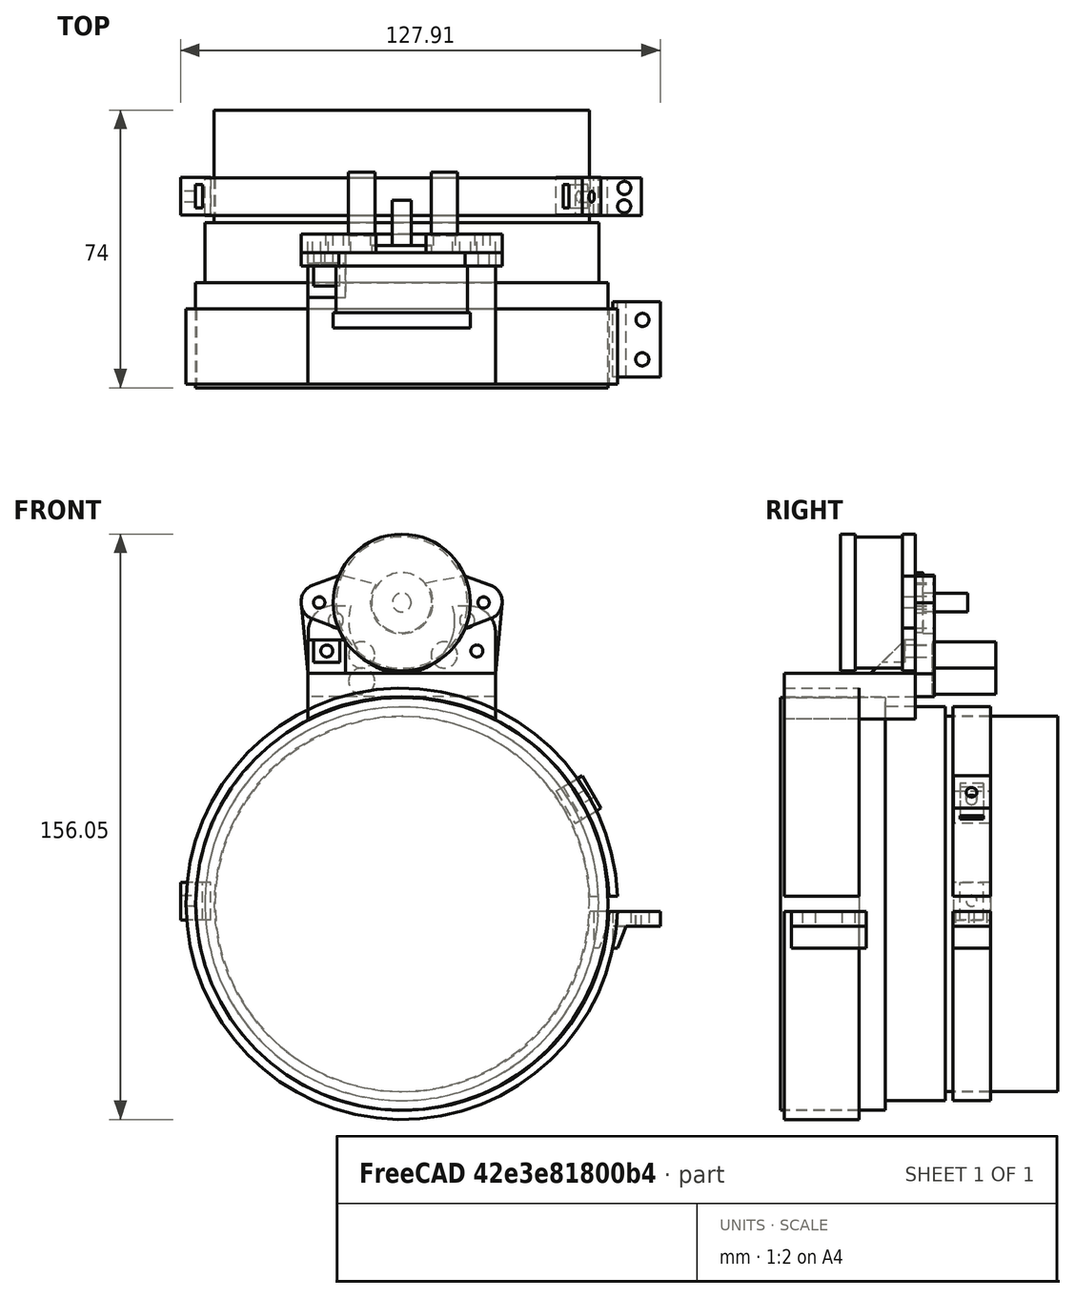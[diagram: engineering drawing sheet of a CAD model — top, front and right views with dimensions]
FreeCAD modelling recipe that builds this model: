
FCSTD DOCUMENT  (FreeCAD 0.18R4 (GitTag))
Label: MTO_3M_6A_500mm
License: All rights reserved
LicenseURL: http://en.wikipedia.org/wiki/All_rights_reserved
objects: Sketcher::SketchObject×30, PartDesign::Body×20, PartDesign::Pad×18, PartDesign::Pocket×12, PartDesign::FeatureBase×8, Mesh::Feature×1, PartDesign::Fillet×1, PartDesign::Plane×1
note: 120 computed .brp shape members not serialized (recipe doc carries the construction recipe); baked Part::Feature solids carry a one-line shape summary decoded from their .brp

FEATURE [Sketcher::SketchObject] Sketch
  MapMode = 5
  Support = -> [XY_Plane]
  sketch-geometry (1):
    g0: Circle CenterX=0.027552 CenterY=0 CenterZ=0 NormalX=0 NormalY=0 NormalZ=1 AngleXU=0 Radius=55
  constraints (1):
    c: Diameter(g0) = 110
FEATURE [PartDesign::Pad] Pad
  Length = 28
  Length2 = 100
  Profile = -> Sketch
  Type = 0
FEATURE [Sketcher::SketchObject] Sketch001
  MapMode = 5
  Placement = pos=(0,0,28) rot=(0,0,1;0rad)
  Support = -> [Pad]
  sketch-geometry (1):
    g0: Circle CenterX=0 CenterY=0 CenterZ=0 NormalX=0 NormalY=0 NormalZ=1 AngleXU=0 Radius=52.5
  constraints (2):
    c: Coincident(g0,g-1)
    c: Diameter(g0) = 105
FEATURE [PartDesign::Pad] Pad001
  BaseFeature = -> Pad
  Length = 16
  Length2 = 100
  Profile = -> Sketch001
  Type = 0
FEATURE [Sketcher::SketchObject] Sketch002
  MapMode = 5
  Placement = pos=(0,0,0) rot=(1,0,0;1.5708rad)
  Support = -> [XZ_Plane001]
  sketch-geometry (1):
    g0: Circle CenterX=0 CenterY=0 CenterZ=0 NormalX=0 NormalY=0 NormalZ=1 AngleXU=0 Radius=57.5
  constraints (2):
    c: Coincident(g0,g-1)
    c: Diameter(g0) = 115
FEATURE [PartDesign::Pad] Pad002
  Length = 20
  Length2 = 100
  Placement = pos=(0,0,0) rot=(1,0,0;1.5708rad)
  Profile = -> Sketch002
  Type = 0
FEATURE [Sketcher::SketchObject] Sketch003
  MapMode = 5
  Placement = pos=(0,-20,8.8e-15) rot=(1,0,0;1.5708rad)
  Support = -> [Pad002]
  sketch-geometry (1):
    g0: Circle CenterX=0.237796 CenterY=-0.12528 CenterZ=0 NormalX=0 NormalY=0 NormalZ=1 AngleXU=0 Radius=55
  constraints (1):
    c: Diameter(g0) = 110
FEATURE [PartDesign::Pocket] Pocket
  BaseFeature = -> Pad002
  Length = 25
  Length2 = 100
  Placement = pos=(0,0,0) rot=(1,0,0;1.5708rad)
  Profile = -> Sketch003
  Type = 0
FEATURE [Sketcher::SketchObject] Sketch004
  MapMode = 5
  Placement = pos=(0,-20,8.8e-15) rot=(1,0,0;1.5708rad)
  Support = -> [Pocket]
  sketch-geometry (4):
    g0: LineSegment StartX=65.8967 StartY=-2 StartZ=0 EndX=0 EndY=-2 EndZ=0
    g1: LineSegment StartX=0 StartY=-2 StartZ=0 EndX=0 EndY=2 EndZ=0
    g2: LineSegment StartX=0 StartY=2 StartZ=0 EndX=65.8967 EndY=2 EndZ=0
    g3: LineSegment StartX=65.8967 StartY=2 StartZ=0 EndX=65.8967 EndY=-2 EndZ=0
  constraints (10):
    c: Coincident(g0,g1)
    c: Coincident(g1,g2)
    c: Coincident(g2,g3)
    c: Coincident(g3,g0)
    c: Horizontal(g0)
    c: Horizontal(g2)
    c: Vertical(g1)
    c: Vertical(g3)
    c: DistanceY(g1,g1) = 4
    c: Symmetric(g0,g1,g-1)
FEATURE [PartDesign::Pocket] Pocket001
  BaseFeature = -> Pocket
  Length = 21
  Length2 = 100
  Placement = pos=(0,0,0) rot=(1,0,0;1.5708rad)
  Profile = -> Sketch004
  Type = 0
FEATURE [PartDesign::Body] Body001  label="01_StepperRing"
  Group = -> [Sketch002,Pad002,Sketch003,Pocket,Sketch004,Pocket001]
  Origin = -> Origin001
  Placement = pos=(0,-2,0) rot=(0,0,1;0rad)
  Tip = -> Pocket001
FEATURE [Mesh::Feature] StepperMotor_scaled  label="REFERENCE_StepperMotor"
  Placement = pos=(-0.0857864,9.5,75.5711) rot=(0,-0.707107,-0.707107;3.14159rad)
FEATURE [Sketcher::SketchObject] Sketch012
  MapMode = 5
  Placement = pos=(0,0,44) rot=(0,0,1;0rad)
  Support = -> [Pad001]
  sketch-geometry (1):
    g0: Circle CenterX=0 CenterY=0 CenterZ=0 NormalX=0 NormalY=0 NormalZ=1 AngleXU=0 Radius=50
  constraints (2):
    c: Coincident(g0,g-1)
    c: Diameter(g0) = 100
FEATURE [PartDesign::Pad] Pad005
  BaseFeature = -> Pad001
  Length = 30
  Length2 = 100
  Profile = -> Sketch012
  Type = 0
FEATURE [PartDesign::Body] Body  label="REFERENCE_Lens"
  Group = -> [Sketch,Pad,Sketch001,Pad001,Sketch012,Pad005]
  Origin = -> Origin
  Placement = pos=(0,-23,5e-15) rot=(-1,0,0;1.5708rad)
  Tip = -> Pad005
FEATURE [Sketcher::SketchObject] Sketch013
  MapMode = 5
  Placement = pos=(0,0,0) rot=(1,0,0;1.5708rad)
  Support = -> [XZ_Plane002]
  sketch-geometry (6):
    g0: LineSegment StartX=68.9137 StartY=6.14746 StartZ=0 EndX=68.9137 EndY=2.14746 EndZ=0
    g1: LineSegment StartX=68.9137 StartY=2.14746 StartZ=0 EndX=56.1787 EndY=2.14746 EndZ=0
    g2: LineSegment StartX=56.1787 StartY=2.14746 StartZ=0 EndX=56.1787 EndY=11.9606 EndZ=0
    g3: LineSegment StartX=68.9137 StartY=6.14746 StartZ=0 EndX=59.8276 EndY=6.14746 EndZ=0
    g4: LineSegment StartX=59.8276 StartY=6.14746 StartZ=0 EndX=57.5381 EndY=11.9606 EndZ=0
    g5: LineSegment StartX=57.5381 StartY=11.9606 StartZ=0 EndX=56.1787 EndY=11.9606 EndZ=0
  constraints (12):
    c: Coincident(g0,g1)
    c: Coincident(g1,g2)
    c: Horizontal(g1)
    c: Vertical(g0)
    c: Vertical(g2)
    c: DistanceY(g0,g0) = 4
    c: Coincident(g0,g3)
    c: Horizontal(g3)
    c: Coincident(g3,g4)
    c: Coincident(g4,g5)
    c: Horizontal(g5)
    c: Coincident(g5,g2)
FEATURE [PartDesign::Pad] Pad006
  Length = 20
  Length2 = 100
  Placement = pos=(0,0,0) rot=(1,0,0;1.5708rad)
  Profile = -> Sketch013
  Type = 0
FEATURE [Sketcher::SketchObject] Sketch014
  MapMode = 5
  Placement = pos=(0,4.1e-15,6.14746) rot=(0,0,1;3.14159rad)
  Support = -> [Pad006]
  sketch-geometry (2):
    g0: Circle CenterX=-64.1611 CenterY=15.2178 CenterZ=0 NormalX=0 NormalY=0 NormalZ=1 AngleXU=0 Radius=1.75
    g1: Circle CenterX=-64.106 CenterY=4.6932 CenterZ=0 NormalX=0 NormalY=0 NormalZ=1 AngleXU=0 Radius=1.75
  constraints (2):
    c: Diameter(g0) = 3.5
    c: Diameter(g1) = 3.5
FEATURE [PartDesign::Pocket] Pocket002
  BaseFeature = -> Pad006
  Length = 5
  Length2 = 100
  Placement = pos=(0,0,0) rot=(1,0,0;1.5708rad)
  Profile = -> Sketch014
  Type = 0
FEATURE [PartDesign::Body] Body002  label="01_StepperClamp1"
  Group = -> [Sketch013,Pad006,Sketch014,Pocket002]
  Origin = -> Origin002
  Placement = pos=(0,0,-0.1) rot=(0,0,1;0rad)
  Tip = -> Pocket002
FEATURE [PartDesign::FeatureBase] Clone
  BaseFeature = -> Body002
FEATURE [PartDesign::Body] Body003  label="01_StepperClamp2"
  BaseFeature = -> Body002
  Group = -> [Clone]
  Origin = -> Origin003
  Placement = pos=(0,-20.1,0.1) rot=(1,0,0;3.14159rad)
  Tip = -> Clone
FEATURE [Sketcher::SketchObject] Sketch035
  MapMode = 5
  Placement = pos=(0,0,0) rot=(1,0,0;1.5708rad)
  Support = -> [XZ_Plane010]
  sketch-geometry (1):
    g0: Circle CenterX=0 CenterY=0 CenterZ=0 NormalX=0 NormalY=0 NormalZ=1 AngleXU=0 Radius=52.5
  constraints (2):
    c: Coincident(g0,g-1)
    c: Diameter(g0) = 105
FEATURE [PartDesign::Pad] Pad012
  Length = 10
  Length2 = 100
  Placement = pos=(0,0,0) rot=(1,0,0;1.5708rad)
  Profile = -> Sketch035
  Type = 0
FEATURE [Sketcher::SketchObject] Sketch034
  MapMode = 5
  Placement = pos=(0,-10,0) rot=(1,0,0;1.5708rad)
  Support = -> [Pad012]
  sketch-geometry (1):
    g0: Circle CenterX=0.237796 CenterY=-0.12528 CenterZ=0 NormalX=0 NormalY=0 NormalZ=1 AngleXU=0 Radius=50
  constraints (1):
    c: Diameter(g0) = 100
FEATURE [PartDesign::Pocket] Pocket006
  BaseFeature = -> Pad012
  Length = 25
  Length2 = 100
  Placement = pos=(0,0,0) rot=(1,0,0;1.5708rad)
  Profile = -> Sketch034
  Type = 0
FEATURE [Sketcher::SketchObject] Sketch033
  MapMode = 5
  Placement = pos=(0,-10,0) rot=(1,0,0;1.5708rad)
  Support = -> [Pocket006]
  sketch-geometry (4):
    g0: LineSegment StartX=65.8967 StartY=-2 StartZ=0 EndX=0 EndY=-2 EndZ=0
    g1: LineSegment StartX=0 StartY=-2 StartZ=0 EndX=0 EndY=2 EndZ=0
    g2: LineSegment StartX=0 StartY=2 StartZ=0 EndX=65.8967 EndY=2 EndZ=0
    g3: LineSegment StartX=65.8967 StartY=2 StartZ=0 EndX=65.8967 EndY=-2 EndZ=0
  constraints (10):
    c: Coincident(g0,g1)
    c: Coincident(g1,g2)
    c: Coincident(g2,g3)
    c: Coincident(g3,g0)
    c: Horizontal(g0)
    c: Horizontal(g2)
    c: Vertical(g1)
    c: Vertical(g3)
    c: DistanceY(g1,g1) = 4
    c: Symmetric(g0,g1,g-1)
FEATURE [PartDesign::Pocket] Pocket007
  BaseFeature = -> Pocket006
  Length = 21
  Length2 = 100
  Placement = pos=(0,0,0) rot=(1,0,0;1.5708rad)
  Profile = -> Sketch033
  Type = 0
FEATURE [PartDesign::Body] Body010  label="02_FocusRing001"
  Group = -> [Sketch035,Pad012,Sketch034,Pocket006,Sketch033,Pocket007]
  Origin = -> Origin010
  Placement = pos=(0,33,0) rot=(0,0,1;0rad)
  Tip = -> Pocket007
FEATURE [Sketcher::SketchObject] Sketch036
  MapMode = 5
  Placement = pos=(0,0,0) rot=(1,0,0;1.5708rad)
  Support = -> [XZ_Plane011]
  sketch-geometry (6):
    g0: LineSegment StartX=68.9137 StartY=6.14746 StartZ=0 EndX=68.9137 EndY=2.14746 EndZ=0
    g1: LineSegment StartX=68.9137 StartY=2.14746 StartZ=0 EndX=56.1787 EndY=2.14746 EndZ=0
    g2: LineSegment StartX=56.1787 StartY=2.14746 StartZ=0 EndX=56.1787 EndY=11.9606 EndZ=0
    g3: LineSegment StartX=68.9137 StartY=6.14746 StartZ=0 EndX=59.8276 EndY=6.14746 EndZ=0
    g4: LineSegment StartX=59.8276 StartY=6.14746 StartZ=0 EndX=57.5381 EndY=11.9606 EndZ=0
    g5: LineSegment StartX=57.5381 StartY=11.9606 StartZ=0 EndX=56.1787 EndY=11.9606 EndZ=0
  constraints (12):
    c: Coincident(g0,g1)
    c: Coincident(g1,g2)
    c: Horizontal(g1)
    c: Vertical(g0)
    c: Vertical(g2)
    c: DistanceY(g0,g0) = 4
    c: Coincident(g0,g3)
    c: Horizontal(g3)
    c: Coincident(g3,g4)
    c: Coincident(g4,g5)
    c: Horizontal(g5)
    c: Coincident(g5,g2)
FEATURE [PartDesign::Pad] Pad013
  Length = 10
  Length2 = 100
  Placement = pos=(0,0,0) rot=(1,0,0;1.5708rad)
  Profile = -> Sketch036
  Type = 0
FEATURE [Sketcher::SketchObject] Sketch037
  MapMode = 5
  Placement = pos=(0,1.4e-15,6.14746) rot=(0,0,1;3.14159rad)
  Support = -> [Pad013]
  sketch-geometry (2):
    g0: Circle CenterX=-64.3315 CenterY=7.29327 CenterZ=0 NormalX=0 NormalY=0 NormalZ=1 AngleXU=0 Radius=1.75
    g1: Circle CenterX=-64.2764 CenterY=2.38916 CenterZ=0 NormalX=0 NormalY=0 NormalZ=1 AngleXU=0 Radius=1.75
  constraints (2):
    c: Diameter(g0) = 3.5
    c: Diameter(g1) = 3.5
FEATURE [PartDesign::Pocket] Pocket008
  BaseFeature = -> Pad013
  Length = 5
  Length2 = 100
  Placement = pos=(0,0,0) rot=(1,0,0;1.5708rad)
  Profile = -> Sketch037
  Type = 0
FEATURE [PartDesign::Body] Body011  label="02_FocusRingClamp1"
  Group = -> [Sketch036,Pad013,Sketch037,Pocket008]
  Origin = -> Origin012
  Placement = pos=(-5,33,-0.1) rot=(0,0,1;0rad)
  Tip = -> Pocket008
FEATURE [PartDesign::FeatureBase] Clone002
  BaseFeature = -> Body011
  Placement = pos=(-5,33,-0.1) rot=(0,0,1;0rad)
FEATURE [PartDesign::Body] Body012  label="02_FocusRingClamp2"
  BaseFeature = -> Body011
  Group = -> [Clone002]
  Origin = -> Origin013
  Placement = pos=(0,56,-7e-15) rot=(1,0,0;3.14159rad)
  Tip = -> Clone002
FEATURE [Sketcher::SketchObject] Sketch038
  MapMode = 5
  Support = -> [XY_Plane013]
  sketch-geometry (4):
    g0: LineSegment StartX=-4.27757 StartY=4.09858 StartZ=0 EndX=5.72243 EndY=4.09858 EndZ=0
    g1: LineSegment StartX=5.72243 StartY=4.09858 StartZ=0 EndX=5.72243 EndY=-5.90142 EndZ=0
    g2: LineSegment StartX=5.72243 StartY=-5.90142 StartZ=0 EndX=-4.27757 EndY=-5.90142 EndZ=0
    g3: LineSegment StartX=-4.27757 StartY=-5.90142 StartZ=0 EndX=-4.27757 EndY=4.09858 EndZ=0
  constraints (10):
    c: Coincident(g0,g1)
    c: Coincident(g1,g2)
    c: Coincident(g2,g3)
    c: Coincident(g3,g0)
    c: Horizontal(g0)
    c: Horizontal(g2)
    c: Vertical(g1)
    c: Vertical(g3)
    c: DistanceX(g0,g0) = 10
    c: DistanceY(g1,g1) = 10
FEATURE [PartDesign::Pad] Pad014
  Length = 8
  Length2 = 100
  Profile = -> Sketch038
  Type = 0
FEATURE [Sketcher::SketchObject] Sketch039
  MapMode = 5
  Placement = pos=(0,0,8) rot=(0,0,1;0rad)
  Support = -> [Pad014]
  sketch-geometry (1):
    g0: Circle CenterX=0.772802 CenterY=-1.02498 CenterZ=0 NormalX=0 NormalY=0 NormalZ=1 AngleXU=0 Radius=1.45
  constraints (1):
    c: Diameter(g0) = 2.9
FEATURE [PartDesign::Pocket] Pocket009
  BaseFeature = -> Pad014
  Length = 5
  Length2 = 100
  Profile = -> Sketch039
  Type = 0
FEATURE [Sketcher::SketchObject] Sketch040
  MapMode = 5
  Placement = pos=(-4.27757,0,0) rot=(0.57735,-0.57735,-0.57735;2.0944rad)
  Support = -> [Pocket009]
  sketch-geometry (4):
    g0: LineSegment StartX=-2.15986 StartY=3.95934 StartZ=0 EndX=4.04014 EndY=3.95934 EndZ=0
    g1: LineSegment StartX=4.04014 StartY=3.95934 StartZ=0 EndX=4.04014 EndY=2.15934 EndZ=0
    g2: LineSegment StartX=4.04014 StartY=2.15934 StartZ=0 EndX=-2.15986 EndY=2.15934 EndZ=0
    g3: LineSegment StartX=-2.15986 StartY=2.15934 StartZ=0 EndX=-2.15986 EndY=3.95934 EndZ=0
  constraints (10):
    c: Coincident(g0,g1)
    c: Coincident(g1,g2)
    c: Coincident(g2,g3)
    c: Coincident(g3,g0)
    c: Horizontal(g0)
    c: Horizontal(g2)
    c: Vertical(g1)
    c: Vertical(g3)
    c: DistanceX(g0,g0) = 6.2
    c: DistanceY(g1,g1) = 1.8
FEATURE [PartDesign::Pocket] Pocket010
  BaseFeature = -> Pocket009
  Length = 15
  Length2 = 100
  Profile = -> Sketch040
  Type = 0
FEATURE [PartDesign::Body] Body013  label="BeltHolder_ORG"
  Group = -> [Sketch038,Pad014,Sketch039,Pocket009,Sketch040,Pocket010]
  Origin = -> Origin014
  Tip = -> Pocket010
FEATURE [PartDesign::FeatureBase] Clone003
  BaseFeature = -> Body013
FEATURE [PartDesign::Body] Body014  label="02_BeltHolder_01_Clone"
  BaseFeature = -> Body013
  Group = -> [Clone003]
  Origin = -> Origin015
  Placement = pos=(43.3038,29,26.4019) rot=(0,1,0;1.0472rad)
  Tip = -> Clone003
FEATURE [PartDesign::FeatureBase] Clone004
  BaseFeature = -> Body013
FEATURE [PartDesign::Body] Body015  label="02_BeltHolder_02_Clone"
  BaseFeature = -> Body013
  Group = -> [Clone004]
  Origin = -> Origin016
  Placement = pos=(-51,29,0) rot=(0,-1,0;1.5708rad)
  Tip = -> Clone004
FEATURE [Sketcher::SketchObject] Sketch042
  MapMode = 5
  Placement = pos=(0,0,0) rot=(1,0,0;1.5708rad)
  Support = -> [XZ_Plane017]
  sketch-geometry (4):
    g0: ArcOfCircle CenterX=0 CenterY=0 CenterZ=0 NormalX=0 NormalY=0 NormalZ=1 AngleXU=0 Radius=55.2351 StartAngle=1.10111 EndAngle=2.04049
    g1: LineSegment StartX=-25 StartY=61.3869 StartZ=0 EndX=25 EndY=61.3869 EndZ=0
    g2: LineSegment StartX=25 StartY=61.3869 StartZ=0 EndX=25 EndY=49.2536 EndZ=0
    g3: LineSegment StartX=-25 StartY=49.2536 StartZ=0 EndX=-25 EndY=61.3869 EndZ=0
  constraints (10):
    c: Coincident(g0,g-1)
    c: Coincident(g1,g2)
    c: Coincident(g3,g1)
    c: Horizontal(g1)
    c: Vertical(g2)
    c: Vertical(g3)
    c: DistanceX(g0,g1) = 25
    c: DistanceX(g1,g0) = 25
    c: Coincident(g0,g3)
    c: Coincident(g0,g2)
FEATURE [PartDesign::Pad] Pad016
  Length = 35
  Length2 = 100
  Midplane = true
  Placement = pos=(0,0,0) rot=(1,0,0;1.5708rad)
  Profile = -> Sketch042
  Reversed = true
  Type = 0
FEATURE [PartDesign::Body] Body017  label="01_StepperRing_AttachPlate"
  Group = -> [Sketch042,Pad016]
  Origin = -> Origin018
  Placement = pos=(0,-4.5,0) rot=(0,0,1;0rad)
  Tip = -> Pad016
FEATURE [Sketcher::SketchObject] Sketch043
  MapMode = 5
  Placement = pos=(0,0,0) rot=(1,0,0;1.5708rad)
  Support = -> [XZ_Plane018]
  sketch-geometry (1):
    g0: Circle CenterX=18.8173 CenterY=57.8472 CenterZ=0 NormalX=0 NormalY=0 NormalZ=1 AngleXU=0 Radius=3.5
  constraints (1):
    c: Diameter(g0) = 7
FEATURE [PartDesign::Pad] Pad017
  Length = 17
  Length2 = 100
  Placement = pos=(0,0,0) rot=(1,0,0;1.5708rad)
  Profile = -> Sketch043
  Reversed = true
  Type = 0
FEATURE [PartDesign::Body] Body018  label="03_BeltWrapper"
  Group = -> [Sketch043,Pad017]
  Origin = -> Origin019
  Placement = pos=(-7.5,17.5,1.5) rot=(0,0,1;0rad)
  Tip = -> Pad017
FEATURE [PartDesign::FeatureBase] Clone005
  BaseFeature = -> Body018
  Placement = pos=(-7.5,17.5,0) rot=(0,0,1;0rad)
FEATURE [PartDesign::Body] Body019  label="03_BeltWrapper_Clone"
  BaseFeature = -> Body018
  Group = -> [Clone005]
  Origin = -> Origin020
  Placement = pos=(-22,0,1.5) rot=(0,0,1;0rad)
  Tip = -> Clone005
FEATURE [Sketcher::SketchObject] Sketch044
  MapMode = 5
  Placement = pos=(0,0,0) rot=(1,0,0;1.5708rad)
  Support = -> [XZ_Plane020]
  sketch-geometry (8):
    g0: ArcOfCircle CenterX=0 CenterY=75.4884 CenterZ=0 NormalX=0 NormalY=0 NormalZ=1 AngleXU=0 Radius=14.1457 StartAngle=2.85425 EndAngle=6.55758
    g1: LineSegment StartX=-24.9269 StartY=79.4974 StartZ=0 EndX=-24.9906 EndY=61.4974 EndZ=0
    g2: LineSegment StartX=24.9776 StartY=61.3214 StartZ=0 EndX=24.9776 EndY=79.3214 EndZ=0
    g3: LineSegment StartX=24.9776 StartY=79.3214 StartZ=0 EndX=13.6165 EndY=79.3214 EndZ=0
    g4: LineSegment StartX=-24.9269 StartY=79.4974 StartZ=0 EndX=-13.5657 EndY=79.4974 EndZ=0
    g5: LineSegment StartX=24.9776 StartY=61.3214 StartZ=0 EndX=24.9776 EndY=55.2035 EndZ=0
    g6: LineSegment StartX=24.9776 StartY=55.2035 StartZ=0 EndX=-24.9906 EndY=55.2035 EndZ=0
    g7: LineSegment StartX=-24.9906 StartY=55.2035 StartZ=0 EndX=-24.9906 EndY=61.4974 EndZ=0
  constraints (18):
    c: PointOnObject(g0,g-2)
    c: Coincident(g2,g3)
    c: Coincident(g3,g0)
    c: Horizontal(g3)
    c: Coincident(g4,g1)
    c: Coincident(g4,g0)
    c: Horizontal(g4)
    c: Equal(g4,g3)
    c: Coincident(g5,g6)
    c: Coincident(g6,g7)
    c: Horizontal(g6)
    c: Vertical(g5)
    c: Vertical(g7)
    c: Coincident(g1,g7)
    c: Coincident(g2,g5)
    c: DistanceY(g1,g1) = 18
    c: DistanceY(g2,g2) = 18
    c: Vertical(g2)
FEATURE [PartDesign::Pad] Pad018
  Length = 5
  Length2 = 100
  Placement = pos=(0,0,0) rot=(1,0,0;1.5708rad)
  Profile = -> Sketch044
  Reversed = true
  Type = 0
FEATURE [PartDesign::Fillet] Fillet
  Base = -> Pad018 [Edge8,Edge1]
  BaseFeature = -> Pad018
  Placement = pos=(0,0,0) rot=(1,0,0;1.5708rad)
  Radius = 7
FEATURE [Sketcher::SketchObject] Sketch045
  MapMode = 5
  Placement = pos=(0,5,-2.2e-15) rot=(-1,0,0;1.5708rad)
  Support = -> [Fillet]
  sketch-geometry (4):
    g0: Circle CenterX=-17.5901 CenterY=-75.5695 CenterZ=0 NormalX=0 NormalY=0 NormalZ=1 AngleXU=0 Radius=2
    g1: Circle CenterX=17.4283 CenterY=-75.5611 CenterZ=0 NormalX=0 NormalY=0 NormalZ=1 AngleXU=0 Radius=2
    g2: Circle CenterX=-20.0024 CenterY=-67.4022 CenterZ=0 NormalX=0 NormalY=0 NormalZ=1 AngleXU=0 Radius=1.6
    g3: Circle CenterX=20.0071 CenterY=-67.4072 CenterZ=0 NormalX=0 NormalY=0 NormalZ=1 AngleXU=0 Radius=1.6
  constraints (4):
    c: Diameter(g0) = 4
    c: Diameter(g1) = 4
    c: Diameter(g3) = 3.2
    c: Diameter(g2) = 3.2
FEATURE [PartDesign::Pocket] Pocket014
  BaseFeature = -> Fillet
  Length = 5
  Length2 = 100
  Placement = pos=(0,0,0) rot=(1,0,0;1.5708rad)
  Profile = -> Sketch045
  Type = 0
FEATURE [PartDesign::Body] Body020  label="03_Alt_28BYJ_StepperPlate"
  Group = -> [Sketch044,Pad018,Fillet,Sketch045,Pocket014]
  Origin = -> Origin021
  Placement = pos=(0,13,0) rot=(0,0,1;0rad)
  Tip = -> Pocket014
FEATURE [Sketcher::SketchObject] Sketch046
  MapMode = 5
  Placement = pos=(0,0,0) rot=(0.57735,0.57735,0.57735;2.0944rad)
  Support = -> [YZ_Plane021]
  sketch-geometry (4):
    g0: LineSegment StartX=13.0313 StartY=70.3749 StartZ=0 EndX=10.2364 EndY=70.3749 EndZ=0
    g1: LineSegment StartX=10.2364 StartY=70.3749 StartZ=0 EndX=1.08443 EndY=61.3909 EndZ=0
    g2: LineSegment StartX=1.08443 StartY=61.3909 StartZ=0 EndX=13.0313 EndY=61.3909 EndZ=0
    g3: LineSegment StartX=13.0313 StartY=61.3909 StartZ=0 EndX=13.0313 EndY=70.3749 EndZ=0
  constraints (7):
    c: Horizontal(g0)
    c: Coincident(g0,g1)
    c: Coincident(g1,g2)
    c: Horizontal(g2)
    c: Coincident(g2,g3)
    c: Coincident(g3,g0)
    c: Vertical(g3)
FEATURE [PartDesign::Pad] Pad019
  Length = 10
  Length2 = 100
  Midplane = true
  Placement = pos=(0,0,0) rot=(0.57735,0.57735,0.57735;2.0944rad)
  Profile = -> Sketch046
  Type = 0
FEATURE [PartDesign::Plane] DatumPlane
  AttachmentOffset = pos=(0,0,1) rot=(0,0,1;0rad)
  Length = 27.3237
  MapMode = 5
  Placement = pos=(-2e-14,3.14e-14,71.3749) rot=(0,0,-1;1.5708rad)
  ResizeMode = 0
  Support = -> [Pad019]
  Width = 24.2924
FEATURE [Sketcher::SketchObject] Sketch047
  MapMode = 5
  Placement = pos=(-2e-14,3.14e-14,71.3749) rot=(0,0,-1;1.5708rad)
  Support = -> [DatumPlane]
  sketch-geometry (4):
    g0: LineSegment StartX=-10.2278 StartY=3.5 StartZ=0 EndX=-2.48035 EndY=3.5 EndZ=0
    g1: LineSegment StartX=-2.48035 StartY=3.5 StartZ=0 EndX=-2.48035 EndY=-3.5 EndZ=0
    g2: LineSegment StartX=-2.48035 StartY=-3.5 StartZ=0 EndX=-10.2278 EndY=-3.5 EndZ=0
    g3: LineSegment StartX=-10.2278 StartY=-3.5 StartZ=0 EndX=-10.2278 EndY=3.5 EndZ=0
  constraints (10):
    c: Coincident(g0,g1)
    c: Coincident(g1,g2)
    c: Coincident(g2,g3)
    c: Coincident(g3,g0)
    c: Horizontal(g0)
    c: Horizontal(g2)
    c: Vertical(g1)
    c: Vertical(g3)
    c: DistanceY(g-1,g0) = 3.5
    c: DistanceY(g3,g3) = 7
FEATURE [PartDesign::Pocket] Pocket015
  BaseFeature = -> Pad019
  Length = 7
  Length2 = 100
  Placement = pos=(0,0,0) rot=(0.57735,0.57735,0.57735;2.0944rad)
  Profile = -> Sketch047
  Type = 0
FEATURE [Sketcher::SketchObject] Sketch048
  MapMode = 5
  Placement = pos=(4.5e-15,10.2278,-5.7e-15) rot=(0.57735,0.57735,-0.57735;2.0944rad)
  Support = -> [Pocket015]
  sketch-geometry (1):
    g0: Circle CenterX=-67.397 CenterY=0 CenterZ=0 NormalX=0 NormalY=0 NormalZ=1 AngleXU=0 Radius=1.6
  constraints (2):
    c: PointOnObject(g0,g-1)
    c: Diameter(g0) = 3.2
FEATURE [PartDesign::Pocket] Pocket016
  BaseFeature = -> Pocket015
  Length = 5
  Length2 = 100
  Placement = pos=(0,0,0) rot=(0.57735,0.57735,0.57735;2.0944rad)
  Profile = -> Sketch048
  Type = 0
FEATURE [PartDesign::Body] Body021  label="01_StepperPlateAttach01"
  Group = -> [Sketch046,Pad019,DatumPlane,Sketch047,Pocket015,Sketch048,Pocket016]
  Origin = -> Origin022
  Placement = pos=(20,0,0) rot=(0,0,1;0rad)
  Tip = -> Pocket016
FEATURE [PartDesign::FeatureBase] Clone006
  BaseFeature = -> Body021
  Placement = pos=(20,0,0) rot=(0,0,1;0rad)
FEATURE [PartDesign::Body] Body022  label="01_StepperPlateAttach02"
  BaseFeature = -> Body021
  Group = -> [Clone006]
  Origin = -> Origin023
  Placement = pos=(-40,0,0) rot=(0,0,1;0rad)
  Tip = -> Clone006
FEATURE [Sketcher::SketchObject] Sketch049
  MapMode = 5
  Placement = pos=(0,5,1e-15) rot=(-1,0,0;1.5708rad)
  sketch-geometry (4):
    g0: Circle CenterX=-22.0296 CenterY=-80.2927 CenterZ=0 NormalX=0 NormalY=0 NormalZ=1 AngleXU=0 Radius=1.75
    g1: Circle CenterX=21.7877 CenterY=-80.2872 CenterZ=0 NormalX=0 NormalY=0 NormalZ=1 AngleXU=0 Radius=1.75
    g2: Circle CenterX=-20.0024 CenterY=-67.4022 CenterZ=0 NormalX=0 NormalY=0 NormalZ=1 AngleXU=0 Radius=1.6
    g3: Circle CenterX=20.0071 CenterY=-67.4072 CenterZ=0 NormalX=0 NormalY=0 NormalZ=1 AngleXU=0 Radius=1.6
  constraints (4):
    c: Diameter(g0) = 3.5
    c: Diameter(g1) = 3.5
    c: Diameter(g3) = 3.2
    c: Diameter(g2) = 3.2
FEATURE [Sketcher::SketchObject] Sketch050
  MapMode = 5
  Placement = pos=(0,0,0) rot=(1,0,0;1.5708rad)
  Support = -> [XZ_Plane023]
  sketch-geometry (14):
    g0: ArcOfCircle CenterX=-0.0193703 CenterY=80.3604 CenterZ=0 NormalX=0 NormalY=0 NormalZ=1 AngleXU=0 Radius=8.35326 StartAngle=2.52193 EndAngle=6.963
    g1: LineSegment StartX=-24.9853 StartY=55.2292 StartZ=0 EndX=24.9928 EndY=55.2292 EndZ=0
    g2: LineSegment StartX=6.47687 StartY=85.6117 StartZ=0 EndX=16.0111 EndY=87.3556 EndZ=0
    g3: LineSegment StartX=16.9297 StartY=87.2712 StartZ=0 EndX=23.9822 EndY=84.5831 EndZ=0
    g4: LineSegment StartX=-23.9798 StartY=84.689 StartZ=0 EndX=-16.8926 EndY=87.451 EndZ=0
    g5: LineSegment StartX=-15.5415 StartY=87.5269 StartZ=0 EndX=-6.81952 EndY=85.2117 EndZ=0
    g6: ArcOfCircle CenterX=-16.1009 CenterY=85.4196 CenterZ=0 NormalX=0 NormalY=0 NormalZ=1 AngleXU=0 Radius=2.18023 StartAngle=1.31133 EndAngle=1.94242
    g7: ArcOfCircle CenterX=22.4308 CenterY=80.5129 CenterZ=0 NormalX=0 NormalY=0 NormalZ=1 AngleXU=0 Radius=4.35582 StartAngle=6.21193 EndAngle=7.48982
    g8: ArcOfCircle CenterX=16.3194 CenterY=85.67 CenterZ=0 NormalX=0 NormalY=0 NormalZ=1 AngleXU=0 Radius=1.71354 StartAngle=1.20664 EndAngle=1.75171
    g9: ArcOfCircle CenterX=-22.3681 CenterY=80.5535 CenterZ=0 NormalX=0 NormalY=0 NormalZ=1 AngleXU=0 Radius=4.4384 StartAngle=1.94242 EndAngle=3.22364
    g10: LineSegment StartX=-26.7915 StartY=80.1898 StartZ=0 EndX=-24.9853 EndY=61.3627 EndZ=0
    g11: LineSegment StartX=-24.9853 StartY=61.3627 StartZ=0 EndX=-24.9853 EndY=55.2292 EndZ=0
    g12: LineSegment StartX=26.7756 StartY=80.2028 StartZ=0 EndX=24.9928 EndY=61.2913 EndZ=0
    g13: LineSegment StartX=24.9928 StartY=61.2913 StartZ=0 EndX=24.9928 EndY=55.2292 EndZ=0
  constraints (17):
    c: Coincident(g0,g2)
    c: Coincident(g5,g0)
    c: Tangent(g4,g6) = 1.5708
    c: Tangent(g5,g6) = 1.5708
    c: Coincident(g12,g7) = -1.5708
    c: Tangent(g3,g7) = 1.5708
    c: Tangent(g2,g8) = 1.5708
    c: Tangent(g3,g8) = 1.5708
    c: Coincident(g10,g9) = -1.5708
    c: Tangent(g4,g9) = 1.5708
    c: Horizontal(g1)
    c: Coincident(g10,g11)
    c: Coincident(g12,g13)
    c: Vertical(g13)
    c: Coincident(g11,g1)
    c: Coincident(g13,g1)
    c: Vertical(g11)
FEATURE [PartDesign::Pad] Pad020
  Length = 5
  Length2 = 100
  Placement = pos=(0,0,0) rot=(1,0,0;1.5708rad)
  Profile = -> Sketch050
  Reversed = true
  Type = 0
FEATURE [PartDesign::Pocket] Pocket017
  BaseFeature = -> Pad020
  Length = 5
  Length2 = 100
  Placement = pos=(0,0,0) rot=(1,0,0;1.5708rad)
  Profile = -> Sketch049
  Type = 0
FEATURE [PartDesign::Body] Body023  label="03_Alt_NEMA14_StepperPlate001"
  Group = -> [Sketch050,Pad020,Sketch049,Pocket017]
  Origin = -> Origin024
  Placement = pos=(0,13,0) rot=(0,0,1;0rad)
  Tip = -> Pocket017
FEATURE [Sketcher::SketchObject] Sketch051
  MapMode = 5
  Support = -> [XY_Plane024]
  sketch-geometry (10):
    g0: ArcOfCircle CenterX=0 CenterY=0 CenterZ=0 NormalX=0 NormalY=0 NormalZ=1 AngleXU=0 Radius=18.25 StartAngle=3.54569 EndAngle=5.88759
    g1: LineSegment StartX=-16.9107 StartY=6.86221 StartZ=0 EndX=-23.6843 EndY=4.41981 EndZ=0
    g2: LineSegment StartX=-23.7033 StartY=-4.64637 StartZ=0 EndX=-16.7801 EndY=-7.17562 EndZ=0
    g3: ArcOfCircle CenterX=-22.0485 CenterY=-0.116735 CenterZ=0 NormalX=0 NormalY=0 NormalZ=1 AngleXU=0 Radius=4.82245 StartAngle=1.91687 EndAngle=4.36212
    g4: LineSegment StartX=16.9474 StartY=6.77103 StartZ=0 EndX=23.6653 EndY=4.27001 EndZ=0
    g5: LineSegment StartX=23.5888 StartY=-4.6513 StartZ=0 EndX=16.8405 EndY=-7.03271 EndZ=0
    g6: ArcOfCircle CenterX=22.0098 CenterY=-0.176776 CenterZ=0 NormalX=0 NormalY=0 NormalZ=1 AngleXU=0 Radius=4.74496 StartAngle=5.05164 EndAngle=7.49759
    g7: Circle CenterX=-22.0152 CenterY=0 CenterZ=0 NormalX=0 NormalY=0 NormalZ=1 AngleXU=0 Radius=1.5
    g8: Circle CenterX=21.8052 CenterY=0 CenterZ=0 NormalX=0 NormalY=0 NormalZ=1 AngleXU=0 Radius=1.5
    g9: ArcOfCircle CenterX=0 CenterY=0 CenterZ=0 NormalX=0 NormalY=0 NormalZ=1 AngleXU=0 Radius=18.25 StartAngle=0.380102 EndAngle=2.7561
  constraints (16):
    c: Coincident(g0,g-1)
    c: Diameter(g0) = 36.5
    c: Tangent(g1,g3) = -1.5708
    c: Tangent(g2,g3) = -1.5708
    c: Coincident(g0,g2)
    c: Coincident(g9,g1)
    c: Tangent(g4,g6) = 1.5708
    c: Tangent(g5,g6) = 1.5708
    c: Diameter(g7) = 3
    c: PointOnObject(g8,g-1)
    c: Diameter(g8) = 3
    c: PointOnObject(g7,g-1)
    c: Equal(g0,g9)
    c: Coincident(g0,g5)
    c: Coincident(g9,g4)
    c: Coincident(g0,g9)
FEATURE [PartDesign::Pad] Pad022
  Length = 3.5
  Length2 = 100
  Profile = -> Sketch051
  Type = 0
FEATURE [Sketcher::SketchObject] Sketch052
  MapMode = 5
  Placement = pos=(0,0,0) rot=(1,0,0;3.14159rad)
  Support = -> [Pad022]
  sketch-geometry (1):
    g0: Circle CenterX=0 CenterY=0 CenterZ=0 NormalX=0 NormalY=0 NormalZ=1 AngleXU=0 Radius=17.5
  constraints (2):
    c: Coincident(g0,g-1)
    c: Diameter(g0) = 35
FEATURE [PartDesign::Pad] Pad003
  BaseFeature = -> Pad022
  Length = 12.5
  Length2 = 100
  Profile = -> Sketch052
  Type = 0
FEATURE [Sketcher::SketchObject] Sketch053
  MapMode = 5
  Placement = pos=(0,0,-12.5) rot=(1,0,0;3.14159rad)
  Support = -> [Pad003]
  sketch-geometry (1):
    g0: Circle CenterX=0 CenterY=0 CenterZ=0 NormalX=0 NormalY=0 NormalZ=1 AngleXU=0 Radius=18.25
  constraints (2):
    c: Coincident(g0,g-1)
    c: Diameter(g0) = 36.5
FEATURE [PartDesign::Pad] Pad004
  BaseFeature = -> Pad003
  Length = 4
  Length2 = 100
  Profile = -> Sketch053
  Type = 0
FEATURE [Sketcher::SketchObject] Sketch005
  MapMode = 5
  Placement = pos=(0,0,3.5) rot=(0,0,1;0rad)
  Support = -> [Pad004]
  sketch-geometry (1):
    g0: Circle CenterX=0 CenterY=0 CenterZ=0 NormalX=0 NormalY=0 NormalZ=1 AngleXU=0 Radius=8
  constraints (2):
    c: Coincident(g0,g-1)
    c: Diameter(g0) = 16
FEATURE [PartDesign::Pad] Pad023
  BaseFeature = -> Pad004
  Length = 2
  Length2 = 100
  Profile = -> Sketch005
  Type = 0
FEATURE [Sketcher::SketchObject] Sketch006
  MapMode = 5
  Placement = pos=(0,0,5.5) rot=(0,0,1;0rad)
  Support = -> [Pad023]
  sketch-geometry (1):
    g0: Circle CenterX=0 CenterY=0 CenterZ=0 NormalX=0 NormalY=0 NormalZ=1 AngleXU=0 Radius=2.5
  constraints (2):
    c: Coincident(g0,g-1)
    c: Diameter(g0) = 5
FEATURE [PartDesign::Pad] Pad021
  BaseFeature = -> Pad023
  Length = 12
  Length2 = 100
  Profile = -> Sketch006
  Type = 0
FEATURE [PartDesign::Body] Body024  label="REFERENCE_Nema14_Round_Pankake"
  Group = -> [Sketch051,Pad022,Sketch052,Pad003,Sketch053,Pad004,Sketch005,Pad023,Sketch006,Pad021]
  Origin = -> Origin025
  Placement = pos=(0,9.5,80.3) rot=(-1,0,0;1.5708rad)
  Tip = -> Pad021
FEATURE [PartDesign::FeatureBase] Clone007
  BaseFeature = -> Body018
  Placement = pos=(-7.5,17.5,1.5) rot=(0,0,1;0rad)
FEATURE [PartDesign::Body] Body025  label="03_Alt_BeltWrapper01_Nema14"
  BaseFeature = -> Body018
  Group = -> [Clone007]
  Origin = -> Origin026
  Placement = pos=(0,0,7) rot=(0,0,1;0rad)
  Tip = -> Clone007
FEATURE [PartDesign::FeatureBase] Clone008
  BaseFeature = -> Body018
  Placement = pos=(-7.5,17.5,1.5) rot=(0,0,1;0rad)
FEATURE [PartDesign::Body] Body026  label="03_Alt_BeltWrapper02_Nema14"
  BaseFeature = -> Body018
  Group = -> [Clone008]
  Origin = -> Origin027
  Placement = pos=(-22,0,7) rot=(0,0,1;0rad)
  Tip = -> Clone008
